# Revit family: RN 90031 Optifitt-Serra-Nippel prolungato
name_source: partatom
category: Rohrformteile
units: mm (PartAtom-declared; Revit-internal decimal feet)

## family parameters
Arbeitsebenenbasiert = Nein
Beim Laden mit Abzugskörper schneiden = Nein
Bemaßung runder Anschluss = Durchmesser verwenden
Gemeinsam genutzt = Nein
Immer vertikal = Ja
Teiletyp = Nicht definiert

## types (12) — shared parameters
1.010.00.2 Blattnummer der Richtlinie = 29
1.010.00.3 Ausgabedatum (Monat) der Richtlinie = 201308
1.010.00.4 Herstellername = R. Nussbaum AG
1.010.00.5 Revisionsdatum der Datei = 20190521
1.010.00.6 Webadresse des Herstellers = http://www.nussbaum.ch
1.100.00.4 Produktbezeichnung = Versorgung
1.110.00.2 Index = 3
1.110.00.4 Produktbezeichnung = Optifitt-Serra
1.960/3L.00.8 Link (URL) = https://www.nussbaum.ch
29.700.00.4 Produktname = Optifitt-Serra-Langnippel
29.700.00.5 Produktkennung = 2
29.700.00.6 Querschnittsform = 1
29.700.00.7 Nennweitensystem = DN
29.700.00.8 Nenndrucksystem = PN
29.710.02.4 Nenndruck = 16
29.710.02.5 max. zul. Überdruck [hPa] = 1600
29.710.02.7 max. zul. Dauer-Betriebsdruck [hPa] = 1600
29.710.02.9 max. zul. Dauer-Betriebstemperatur [°C] = 90
Connector Visibility = Nein
EnclosingSpace Visibility = Nein
R. Nussbaum AG 90031.31 de Visibility = Nein
R. Nussbaum AG 90031.33 de Visibility = Nein
R. Nussbaum AG 90031.41 de Visibility = Nein
R. Nussbaum AG 90031.51 de Visibility = Nein
R. Nussbaum AG 90031.59 de Visibility = Nein

## per-type parameters (varying)
- DN=25: 1.800.00.3 TGA-Nummer=01900300000000000000000000000000000000000000000018000000000000000016; 1.800.00.4 Kommentarfeld=90031.57, Optifitt-Serra-Langnippel, DN=25, L=100; 1.810.00.3 Hersteller-Bestellnummer=90031.57; 1.810.00.4 DATANORM-Nummer=90031.57; 1.810.00.6 GTIN-Nummer=7612945034137; 29.710.02.10 Formstück-Gewicht [kg]=0.28; 29.710.02.3 Benennung=Optifitt-Serra-Langnippel, DN=25, L=100; CONNECTOR0_DIAMETER_dX_0r=25 mm  [stored 0.082021 ft]; CONNECTOR0_dX_01=17 mm  [stored 0.0557743 ft]; CONNECTOR0_ref_dX=17 mm  [stored 0.0557743 ft]; CONNECTOR1_DIAMETER_dX_0r=25 mm  [stored 0.082021 ft]; CONNECTOR1_dX_00=81 mm  [stored 0.265748 ft]; CONNECTOR1_dX_01=98 mm; CONNECTOR1_ref_dX=81 mm  [stored 0.265748 ft]; CONNECTOR1_ref_dX2=98 mm; R. Nussbaum AG 90031.21 de Visibility=Nein; R. Nussbaum AG 90031.23 de Visibility=Nein; R. Nussbaum AG 90031.35 de Visibility=Nein; R. Nussbaum AG 90031.37 de Visibility=Nein; R. Nussbaum AG 90031.39 de Visibility=Nein; R. Nussbaum AG 90031.43 de Visibility=Nein; R. Nussbaum AG 90031.45 de Visibility=Nein; R. Nussbaum AG 90031.47 de Visibility=Nein; R. Nussbaum AG 90031.49 de Visibility=Nein; R. Nussbaum AG 90031.53 de Visibility=Nein; R. Nussbaum AG 90031.55 de Visibility=Nein; R. Nussbaum AG 90031.57 de Visibility=Ja
- DN=7: 1.800.00.3 TGA-Nummer=01900300000000000000000000000000000000000000000018000000000000000015; 1.800.00.4 Kommentarfeld=90031.55, Optifitt-Serra-Langnippel, DN=25, L=80; 1.810.00.3 Hersteller-Bestellnummer=90031.55; 1.810.00.4 DATANORM-Nummer=90031.55; 1.810.00.6 GTIN-Nummer=7612945034120; 29.710.02.10 Formstück-Gewicht [kg]=0.22; 29.710.02.3 Benennung=Optifitt-Serra-Langnippel, DN=25, L=80; CONNECTOR0_DIAMETER_dX_0r=25 mm  [stored 0.082021 ft]; CONNECTOR0_dX_01=17 mm  [stored 0.0557743 ft]; CONNECTOR0_ref_dX=17 mm  [stored 0.0557743 ft]; CONNECTOR1_DIAMETER_dX_0r=25 mm  [stored 0.082021 ft]; CONNECTOR1_dX_00=61 mm; CONNECTOR1_dX_01=78 mm; CONNECTOR1_ref_dX=61 mm; CONNECTOR1_ref_dX2=78 mm; Hersteller=R. Nussbaum AG; Modell=90031.55; R. Nussbaum AG 90031.21 de Visibility=Nein; R. Nussbaum AG 90031.23 de Visibility=Nein; R. Nussbaum AG 90031.35 de Visibility=Nein; R. Nussbaum AG 90031.37 de Visibility=Nein; R. Nussbaum AG 90031.39 de Visibility=Nein; R. Nussbaum AG 90031.43 de Visibility=Nein; R. Nussbaum AG 90031.45 de Visibility=Nein; R. Nussbaum AG 90031.47 de Visibility=Nein; R. Nussbaum AG 90031.49 de Visibility=Nein; R. Nussbaum AG 90031.53 de Visibility=Nein; R. Nussbaum AG 90031.55 de Visibility=Ja; R. Nussbaum AG 90031.57 de Visibility=Nein; Typenkommentare=Optifitt-Serra-Nippel prolungato DN=25; URL=https://www.nussbaum.ch
- DN=8: 1.800.00.3 TGA-Nummer=01900300000000000000000000000000000000000000000018000000000000000014; 1.800.00.4 Kommentarfeld=90031.53, Optifitt-Serra-Langnippel, DN=25, L=60; 1.810.00.3 Hersteller-Bestellnummer=90031.53; 1.810.00.4 DATANORM-Nummer=90031.53; 1.810.00.6 GTIN-Nummer=7612945034113; 29.710.02.10 Formstück-Gewicht [kg]=0.161; 29.710.02.3 Benennung=Optifitt-Serra-Langnippel, DN=25, L=60; CONNECTOR0_DIAMETER_dX_0r=25 mm  [stored 0.082021 ft]; CONNECTOR0_dX_01=17 mm  [stored 0.0557743 ft]; CONNECTOR0_ref_dX=17 mm  [stored 0.0557743 ft]; CONNECTOR1_DIAMETER_dX_0r=25 mm  [stored 0.082021 ft]; CONNECTOR1_dX_00=41 mm  [stored 0.134514 ft]; CONNECTOR1_dX_01=58 mm  [stored 0.190289 ft]; CONNECTOR1_ref_dX=41 mm  [stored 0.134514 ft]; CONNECTOR1_ref_dX2=58 mm  [stored 0.190289 ft]; Hersteller=R. Nussbaum AG; Modell=90031.53; R. Nussbaum AG 90031.21 de Visibility=Nein; R. Nussbaum AG 90031.23 de Visibility=Nein; R. Nussbaum AG 90031.35 de Visibility=Nein; R. Nussbaum AG 90031.37 de Visibility=Nein; R. Nussbaum AG 90031.39 de Visibility=Nein; R. Nussbaum AG 90031.43 de Visibility=Nein; R. Nussbaum AG 90031.45 de Visibility=Nein; R. Nussbaum AG 90031.47 de Visibility=Nein; R. Nussbaum AG 90031.49 de Visibility=Nein; R. Nussbaum AG 90031.53 de Visibility=Ja; R. Nussbaum AG 90031.55 de Visibility=Nein; R. Nussbaum AG 90031.57 de Visibility=Nein; Typenkommentare=Optifitt-Serra-Nippel prolungato DN=25; URL=https://www.nussbaum.ch
- DN=4: 1.800.00.3 TGA-Nummer=01900300000000000000000000000000000000000000000018000000000000000012; 1.800.00.4 Kommentarfeld=90031.49, Optifitt-Serra-Langnippel, DN=20, L=120; 1.810.00.3 Hersteller-Bestellnummer=90031.49; 1.810.00.4 DATANORM-Nummer=90031.49; 1.810.00.6 GTIN-Nummer=7612945034090; 29.710.02.10 Formstück-Gewicht [kg]=0.216; 29.710.02.3 Benennung=Optifitt-Serra-Langnippel, DN=20, L=120; CONNECTOR0_DIAMETER_dX_0r=20 mm; CONNECTOR0_dX_01=15 mm  [stored 0.0492126 ft]; CONNECTOR0_ref_dX=15 mm  [stored 0.0492126 ft]; CONNECTOR1_DIAMETER_dX_0r=20 mm; CONNECTOR1_dX_00=103 mm  [stored 0.337927 ft]; CONNECTOR1_dX_01=118 mm; CONNECTOR1_ref_dX=103 mm  [stored 0.337927 ft]; CONNECTOR1_ref_dX2=118 mm; Hersteller=R. Nussbaum AG; Modell=90031.49; R. Nussbaum AG 90031.21 de Visibility=Nein; R. Nussbaum AG 90031.23 de Visibility=Nein; R. Nussbaum AG 90031.35 de Visibility=Nein; R. Nussbaum AG 90031.37 de Visibility=Nein; R. Nussbaum AG 90031.39 de Visibility=Nein; R. Nussbaum AG 90031.43 de Visibility=Nein; R. Nussbaum AG 90031.45 de Visibility=Nein; R. Nussbaum AG 90031.47 de Visibility=Nein; R. Nussbaum AG 90031.49 de Visibility=Ja; R. Nussbaum AG 90031.53 de Visibility=Nein; R. Nussbaum AG 90031.55 de Visibility=Nein; R. Nussbaum AG 90031.57 de Visibility=Nein; Typenkommentare=Optifitt-Serra-Nippel prolungato DN=20; URL=https://www.nussbaum.ch
- DN=6: 1.800.00.3 TGA-Nummer=01900300000000000000000000000000000000000000000018000000000000000011; 1.800.00.4 Kommentarfeld=90031.47, Optifitt-Serra-Langnippel, DN=20, L=100; 1.810.00.3 Hersteller-Bestellnummer=90031.47; 1.810.00.4 DATANORM-Nummer=90031.47; 1.810.00.6 GTIN-Nummer=7612945034083; 29.710.02.10 Formstück-Gewicht [kg]=0.179; 29.710.02.3 Benennung=Optifitt-Serra-Langnippel, DN=20, L=100; CONNECTOR0_DIAMETER_dX_0r=20 mm; CONNECTOR0_dX_01=15 mm  [stored 0.0492126 ft]; CONNECTOR0_ref_dX=15 mm  [stored 0.0492126 ft]; CONNECTOR1_DIAMETER_dX_0r=20 mm; CONNECTOR1_dX_00=83 mm; CONNECTOR1_dX_01=98 mm; CONNECTOR1_ref_dX=83 mm; CONNECTOR1_ref_dX2=98 mm; Hersteller=R. Nussbaum AG; Modell=90031.47; R. Nussbaum AG 90031.21 de Visibility=Nein; R. Nussbaum AG 90031.23 de Visibility=Nein; R. Nussbaum AG 90031.35 de Visibility=Nein; R. Nussbaum AG 90031.37 de Visibility=Nein; R. Nussbaum AG 90031.39 de Visibility=Nein; R. Nussbaum AG 90031.43 de Visibility=Nein; R. Nussbaum AG 90031.45 de Visibility=Nein; R. Nussbaum AG 90031.47 de Visibility=Ja; R. Nussbaum AG 90031.49 de Visibility=Nein; R. Nussbaum AG 90031.53 de Visibility=Nein; R. Nussbaum AG 90031.55 de Visibility=Nein; R. Nussbaum AG 90031.57 de Visibility=Nein; Typenkommentare=Optifitt-Serra-Nippel prolungato DN=20; URL=https://www.nussbaum.ch
- DN=5: 1.800.00.3 TGA-Nummer=01900300000000000000000000000000000000000000000018000000000000000010; 1.800.00.4 Kommentarfeld=90031.45, Optifitt-Serra-Langnippel, DN=20, L=80; 1.810.00.3 Hersteller-Bestellnummer=90031.45; 1.810.00.4 DATANORM-Nummer=90031.45; 1.810.00.6 GTIN-Nummer=7612945034076; 29.710.02.10 Formstück-Gewicht [kg]=0.144; 29.710.02.3 Benennung=Optifitt-Serra-Langnippel, DN=20, L=80; CONNECTOR0_DIAMETER_dX_0r=20 mm; CONNECTOR0_dX_01=15 mm  [stored 0.0492126 ft]; CONNECTOR0_ref_dX=15 mm  [stored 0.0492126 ft]; CONNECTOR1_DIAMETER_dX_0r=20 mm; CONNECTOR1_dX_00=63 mm; CONNECTOR1_dX_01=78 mm; CONNECTOR1_ref_dX=63 mm; CONNECTOR1_ref_dX2=78 mm; Hersteller=R. Nussbaum AG; Modell=90031.45; R. Nussbaum AG 90031.21 de Visibility=Nein; R. Nussbaum AG 90031.23 de Visibility=Nein; R. Nussbaum AG 90031.35 de Visibility=Nein; R. Nussbaum AG 90031.37 de Visibility=Nein; R. Nussbaum AG 90031.39 de Visibility=Nein; R. Nussbaum AG 90031.43 de Visibility=Nein; R. Nussbaum AG 90031.45 de Visibility=Ja; R. Nussbaum AG 90031.47 de Visibility=Nein; R. Nussbaum AG 90031.49 de Visibility=Nein; R. Nussbaum AG 90031.53 de Visibility=Nein; R. Nussbaum AG 90031.55 de Visibility=Nein; R. Nussbaum AG 90031.57 de Visibility=Nein; Typenkommentare=Optifitt-Serra-Nippel prolungato DN=20; URL=https://www.nussbaum.ch
- DN=20: 1.800.00.3 TGA-Nummer=01900300000000000000000000000000000000000000000018000000000000000009; 1.800.00.4 Kommentarfeld=90031.43, Optifitt-Serra-Langnippel, DN=20, L=60; 1.810.00.3 Hersteller-Bestellnummer=90031.43; 1.810.00.4 DATANORM-Nummer=90031.43; 1.810.00.6 GTIN-Nummer=7612945034069; 29.710.02.10 Formstück-Gewicht [kg]=0.108; 29.710.02.3 Benennung=Optifitt-Serra-Langnippel, DN=20, L=60; CONNECTOR0_DIAMETER_dX_0r=20 mm; CONNECTOR0_dX_01=15 mm  [stored 0.0492126 ft]; CONNECTOR0_ref_dX=15 mm  [stored 0.0492126 ft]; CONNECTOR1_DIAMETER_dX_0r=20 mm; CONNECTOR1_dX_00=43 mm  [stored 0.141076 ft]; CONNECTOR1_dX_01=58 mm  [stored 0.190289 ft]; CONNECTOR1_ref_dX=43 mm  [stored 0.141076 ft]; CONNECTOR1_ref_dX2=58 mm  [stored 0.190289 ft]; Hersteller=R. Nussbaum AG; Modell=90031.43; R. Nussbaum AG 90031.21 de Visibility=Nein; R. Nussbaum AG 90031.23 de Visibility=Nein; R. Nussbaum AG 90031.35 de Visibility=Nein; R. Nussbaum AG 90031.37 de Visibility=Nein; R. Nussbaum AG 90031.39 de Visibility=Nein; R. Nussbaum AG 90031.43 de Visibility=Ja; R. Nussbaum AG 90031.45 de Visibility=Nein; R. Nussbaum AG 90031.47 de Visibility=Nein; R. Nussbaum AG 90031.49 de Visibility=Nein; R. Nussbaum AG 90031.53 de Visibility=Nein; R. Nussbaum AG 90031.55 de Visibility=Nein; R. Nussbaum AG 90031.57 de Visibility=Nein; Typenkommentare=Optifitt-Serra-Nippel prolungato DN=20; URL=https://www.nussbaum.ch
- DN=2: 1.800.00.3 TGA-Nummer=01900300000000000000000000000000000000000000000018000000000000000007; 1.800.00.4 Kommentarfeld=90031.39, Optifitt-Serra-Langnippel, DN=15, L=120; 1.810.00.3 Hersteller-Bestellnummer=90031.39; 1.810.00.4 DATANORM-Nummer=90031.39; 1.810.00.6 GTIN-Nummer=7612945034045; 29.710.02.10 Formstück-Gewicht [kg]=0.16; 29.710.02.3 Benennung=Optifitt-Serra-Langnippel, DN=15, L=120; CONNECTOR0_DIAMETER_dX_0r=15 mm  [stored 0.0492126 ft]; CONNECTOR0_dX_01=13 mm; CONNECTOR0_ref_dX=13 mm; CONNECTOR1_DIAMETER_dX_0r=15 mm  [stored 0.0492126 ft]; CONNECTOR1_dX_00=105 mm; CONNECTOR1_dX_01=118 mm; CONNECTOR1_ref_dX=105 mm; CONNECTOR1_ref_dX2=118 mm; Hersteller=R. Nussbaum AG; Modell=90031.39; R. Nussbaum AG 90031.21 de Visibility=Nein; R. Nussbaum AG 90031.23 de Visibility=Nein; R. Nussbaum AG 90031.35 de Visibility=Nein; R. Nussbaum AG 90031.37 de Visibility=Nein; R. Nussbaum AG 90031.39 de Visibility=Ja; R. Nussbaum AG 90031.43 de Visibility=Nein; R. Nussbaum AG 90031.45 de Visibility=Nein; R. Nussbaum AG 90031.47 de Visibility=Nein; R. Nussbaum AG 90031.49 de Visibility=Nein; R. Nussbaum AG 90031.53 de Visibility=Nein; R. Nussbaum AG 90031.55 de Visibility=Nein; R. Nussbaum AG 90031.57 de Visibility=Nein; Typenkommentare=Optifitt-Serra-Nippel prolungato DN=15; URL=https://www.nussbaum.ch
- DN=15: 1.800.00.3 TGA-Nummer=01900300000000000000000000000000000000000000000018000000000000000006; 1.800.00.4 Kommentarfeld=90031.37, Optifitt-Serra-Langnippel, DN=15, L=100; 1.810.00.3 Hersteller-Bestellnummer=90031.37; 1.810.00.4 DATANORM-Nummer=90031.37; 1.810.00.6 GTIN-Nummer=7612945034038; 29.710.02.10 Formstück-Gewicht [kg]=0.14; 29.710.02.3 Benennung=Optifitt-Serra-Langnippel, DN=15, L=100; CONNECTOR0_DIAMETER_dX_0r=15 mm  [stored 0.0492126 ft]; CONNECTOR0_dX_01=13 mm; CONNECTOR0_ref_dX=13 mm; CONNECTOR1_DIAMETER_dX_0r=15 mm  [stored 0.0492126 ft]; CONNECTOR1_dX_00=85 mm; CONNECTOR1_dX_01=98 mm; CONNECTOR1_ref_dX=85 mm; CONNECTOR1_ref_dX2=98 mm; Hersteller=R. Nussbaum AG; Modell=90031.37; R. Nussbaum AG 90031.21 de Visibility=Nein; R. Nussbaum AG 90031.23 de Visibility=Nein; R. Nussbaum AG 90031.35 de Visibility=Nein; R. Nussbaum AG 90031.37 de Visibility=Ja; R. Nussbaum AG 90031.39 de Visibility=Nein; R. Nussbaum AG 90031.43 de Visibility=Nein; R. Nussbaum AG 90031.45 de Visibility=Nein; R. Nussbaum AG 90031.47 de Visibility=Nein; R. Nussbaum AG 90031.49 de Visibility=Nein; R. Nussbaum AG 90031.53 de Visibility=Nein; R. Nussbaum AG 90031.55 de Visibility=Nein; R. Nussbaum AG 90031.57 de Visibility=Nein; Typenkommentare=Optifitt-Serra-Nippel prolungato DN=15; URL=https://www.nussbaum.ch
- DN=3: 1.800.00.3 TGA-Nummer=01900300000000000000000000000000000000000000000018000000000000000005; 1.800.00.4 Kommentarfeld=90031.35, Optifitt-Serra-Langnippel, DN=15, L=80; 1.810.00.3 Hersteller-Bestellnummer=90031.35; 1.810.00.4 DATANORM-Nummer=90031.35; 1.810.00.6 GTIN-Nummer=7612945034021; 29.710.02.10 Formstück-Gewicht [kg]=0.106; 29.710.02.3 Benennung=Optifitt-Serra-Langnippel, DN=15, L=80; CONNECTOR0_DIAMETER_dX_0r=15 mm  [stored 0.0492126 ft]; CONNECTOR0_dX_01=13 mm; CONNECTOR0_ref_dX=13 mm; CONNECTOR1_DIAMETER_dX_0r=15 mm  [stored 0.0492126 ft]; CONNECTOR1_dX_00=65 mm; CONNECTOR1_dX_01=78 mm; CONNECTOR1_ref_dX=65 mm; CONNECTOR1_ref_dX2=78 mm; Hersteller=R. Nussbaum AG; Modell=90031.35; R. Nussbaum AG 90031.21 de Visibility=Nein; R. Nussbaum AG 90031.23 de Visibility=Nein; R. Nussbaum AG 90031.35 de Visibility=Ja; R. Nussbaum AG 90031.37 de Visibility=Nein; R. Nussbaum AG 90031.39 de Visibility=Nein; R. Nussbaum AG 90031.43 de Visibility=Nein; R. Nussbaum AG 90031.45 de Visibility=Nein; R. Nussbaum AG 90031.47 de Visibility=Nein; R. Nussbaum AG 90031.49 de Visibility=Nein; R. Nussbaum AG 90031.53 de Visibility=Nein; R. Nussbaum AG 90031.55 de Visibility=Nein; R. Nussbaum AG 90031.57 de Visibility=Nein; Typenkommentare=Optifitt-Serra-Nippel prolungato DN=15; URL=https://www.nussbaum.ch
- DN=1: 1.800.00.3 TGA-Nummer=01900300000000000000000000000000000000000000000018000000000000000002; 1.800.00.4 Kommentarfeld=90031.23, Optifitt-Serra-Langnippel, DN=10, L=60; 1.810.00.3 Hersteller-Bestellnummer=90031.23; 1.810.00.4 DATANORM-Nummer=90031.23; 1.810.00.6 GTIN-Nummer=7612945033963; 29.710.02.10 Formstück-Gewicht [kg]=0.04; 29.710.02.3 Benennung=Optifitt-Serra-Langnippel, DN=10, L=60; CONNECTOR0_DIAMETER_dX_0r=10 mm  [stored 0.0328084 ft]; CONNECTOR0_dX_01=10 mm  [stored 0.0328084 ft]; CONNECTOR0_ref_dX=10 mm  [stored 0.0328084 ft]; CONNECTOR1_DIAMETER_dX_0r=10 mm  [stored 0.0328084 ft]; CONNECTOR1_dX_00=48 mm; CONNECTOR1_dX_01=58 mm  [stored 0.190289 ft]; CONNECTOR1_ref_dX=48 mm; CONNECTOR1_ref_dX2=58 mm  [stored 0.190289 ft]; Hersteller=R. Nussbaum AG; Modell=90031.23; R. Nussbaum AG 90031.21 de Visibility=Nein; R. Nussbaum AG 90031.23 de Visibility=Ja; R. Nussbaum AG 90031.35 de Visibility=Nein; R. Nussbaum AG 90031.37 de Visibility=Nein; R. Nussbaum AG 90031.39 de Visibility=Nein; R. Nussbaum AG 90031.43 de Visibility=Nein; R. Nussbaum AG 90031.45 de Visibility=Nein; R. Nussbaum AG 90031.47 de Visibility=Nein; R. Nussbaum AG 90031.49 de Visibility=Nein; R. Nussbaum AG 90031.53 de Visibility=Nein; R. Nussbaum AG 90031.55 de Visibility=Nein; R. Nussbaum AG 90031.57 de Visibility=Nein; Typenkommentare=Optifitt-Serra-Nippel prolungato DN=10; URL=https://www.nussbaum.ch
- DN=10: 1.800.00.3 TGA-Nummer=01900300000000000000000000000000000000000000000018000000000000000001; 1.800.00.4 Kommentarfeld=90031.21, Optifitt-Serra-Langnippel, DN=10, L=40; 1.810.00.3 Hersteller-Bestellnummer=90031.21; 1.810.00.4 DATANORM-Nummer=90031.21; 1.810.00.6 GTIN-Nummer=7612945033956; 29.710.02.10 Formstück-Gewicht [kg]=0.02; 29.710.02.3 Benennung=Optifitt-Serra-Langnippel, DN=10, L=40; CONNECTOR0_DIAMETER_dX_0r=10 mm  [stored 0.0328084 ft]; CONNECTOR0_dX_01=10 mm  [stored 0.0328084 ft]; CONNECTOR0_ref_dX=10 mm  [stored 0.0328084 ft]; CONNECTOR1_DIAMETER_dX_0r=10 mm  [stored 0.0328084 ft]; CONNECTOR1_dX_00=28 mm; CONNECTOR1_dX_01=38 mm; CONNECTOR1_ref_dX=28 mm; CONNECTOR1_ref_dX2=38 mm; Hersteller=R. Nussbaum AG; Modell=90031.21; R. Nussbaum AG 90031.21 de Visibility=Ja; R. Nussbaum AG 90031.23 de Visibility=Nein; R. Nussbaum AG 90031.35 de Visibility=Nein; R. Nussbaum AG 90031.37 de Visibility=Nein; R. Nussbaum AG 90031.39 de Visibility=Nein; R. Nussbaum AG 90031.43 de Visibility=Nein; R. Nussbaum AG 90031.45 de Visibility=Nein; R. Nussbaum AG 90031.47 de Visibility=Nein; R. Nussbaum AG 90031.49 de Visibility=Nein; R. Nussbaum AG 90031.53 de Visibility=Nein; R. Nussbaum AG 90031.55 de Visibility=Nein; R. Nussbaum AG 90031.57 de Visibility=Nein; Typenkommentare=Optifitt-Serra-Nippel prolungato DN=10; URL=https://www.nussbaum.ch

note: [stored X ft] marks values corroborated as IEEE doubles in the binary element streams (Revit-internal decimal feet)

## geometry (parser evidence)
native form markers: Sweep x3
no freeform markers — native parametric forms only
